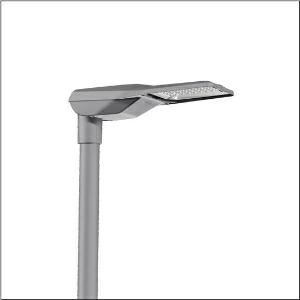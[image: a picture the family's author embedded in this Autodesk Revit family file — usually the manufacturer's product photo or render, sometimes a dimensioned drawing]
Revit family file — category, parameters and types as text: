
# Revit family: streetlight_sl_21_iq_mini___stw1_0a_5xe2e21g08hb_26c4
name_source: partatom
category: Lighting Fixtures
units: mm (PartAtom-declared; Revit-internal decimal feet)

## family parameters
Cut with Voids When Loaded = No
Host = Face
Light Source = No
Part Type = Normal
Room Calculation Point = No
Round Connector Dimension = Use Diameter
Shared = No

## types (1)
- --- (1 x LED, 7830 lm, 70.9 W, 2200K)
    Apparent Load = 71 VA
    CIE Flux Codes = 38 75 98 100 100
    Color Rendering = 70
    Color Temperature = 2200K
    Default Elevation = 1800 mm
    Description = Streetlight SL 21 iQ mini, mast luminaire, primary light control with lens, of PMMA, primary optical cover: cover, of toughened safety glass, transparent, light distribution: STW1.0a, light emission: direct distribution, primary light characteristic: asymmetric, installation type: post-top, side-entry, LED, High Power LED, rated luminous flux: 7.830lm, luminous efficacy: 110lm/W, light colour: 722, colour temperature: 2200K, control: Street-Remote, Auto-Match, Temp-Guard, Lumen-Switch, Night-Set, Smart-Wire, Light-Fading, Desk-Remote (wireless, voltage-free reading and setting of iQ features in the workshop via application-optimized NFC function/RFID function), optimised constant luminous flux control (CLO 2.0), presetting dimming linear, mains connection: 220..240V, AC, 50/60Hz, start of lifetime: 71W, end of service life: 75W, reduction: 31W, luminaire housing, of diecast aluminium, powder-coated, Siteco® metallic grey (DB 702S), corrosivity category C5 mid according to DIN EN ISO 12944, please order mast flange separately, inclination adjustable: 0°, 5°, 10°, 15°, sealing non-destructively replaceable, multi-level sealing system, length: 628mm, width: 235mm, height: 110mm, mast flange for spigot size: 42mm (side-entry): 5XC10008XM4, 60/48mm (side-entry/post-top): 5XC10108XM2, 76/60mm (side-entry/post-top): 5XC10108XM1, protection rating (complete): IP66, insulation class (complete): insulation class II (safety insulation), certification: CE, ENEC, ENEC+, VDE, impact resistance: IK09, permissible operating ambient temperature for outdoor applications: -40..+50°C, standard-compliant lighting for roads and squares, packaging unit: 1 piece

Light Distribution: STW1.0a
    Height = 110 mm
    Lamp = 1 x LED
    Lamp Light Flux = 7830 lm
    Lamp Power = 70.9 W
    Lamp count = 1
    Length = 625 mm
    Luminous efficacy = 110 lm/W
    Manufacturer = Siteco
    ModVariant = No
    Model = 5XE2E21G08HB
    Number of Poles = 1
    OnlyDefault = Yes
    Power Factor = 1
    Product Name = Streetlight SL 21 iQ mini | STW1.0a
    Product group = mast luminaire | pylon top
    ProductGroupID = 6100
    Protection Class = Protection class II
    Protection Degree = IP 66
    RLX_Detail_Level = 1
    RLX_Emergency_Light_Flux = 0 lm
    RLX_Emergency_Type = 0
    RLX_Emergency_Type_DB = No
    RlxData = <blob elided: 91977 chars, md5=706b8a17>
    Socket = socket
    Standby Power = 0 W
    System Light Flux = 7830 lm
    System Power = 71 W
    Type Comments = factory setting: luminous flux: 100 % | dim-lin: 254 | 711 mA
    Type Image = l_1003519.jpg
    URL = http://relux.com
    VarID = @adj_090305
    Voltage = 0 V
    Weight = 0.00 kg
    Width = 234 mm

## geometry (parser evidence)
native form markers: Blend x4, Sweep x9
no freeform markers — native parametric forms only
